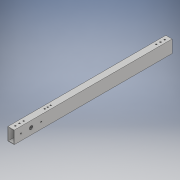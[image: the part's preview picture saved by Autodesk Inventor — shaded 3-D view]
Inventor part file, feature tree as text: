
AUTODESK INVENTOR PART (.ipt)
format: ipt  version: 2019 (Build 230136000, 136)  size: 197,120 bytes
history: native  units: mm
features: sketch x9, extrude x5, hole x3, other x1
ambient origin geometry x8: Origin, YZ Plane, XZ Plane, XY Plane, X Axis, Y Axis, Z Axis, Center Point
bodies: Body1 (feature_tree)
feature tree (18):
  other  "ソリッド1"
  extrude  "押し出し1"  Depth=15.0mm
  hole  "穴1"  [1 undecoded]
  hole  "穴2"  [1 undecoded]
  extrude  "押し出し2"  Depth=28.0mm
  sketch  "スケッチ5"
  extrude  "押し出し3"  Depth=1.0mm
  extrude  "押し出し4"  Depth=1.0mm
  extrude  "押し出し5"  Depth=375.0mm TaperAngle=0.0deg
  hole  "穴3"  [1 undecoded]
  sketch  "スケッチ1"
  sketch  "スケッチ2"
  sketch  "スケッチ3"
  sketch  "スケッチ4"
  sketch  "スケッチ6"
  sketch  "スケッチ7"
  sketch  "スケッチ8"
  sketch  "スケッチ9"
note: 3 required parameter values undecoded (feature->parameter linkage not recoverable at this tier; creation-order binding heuristic only, values carry confidence <= 0.55)
